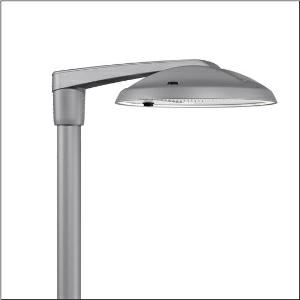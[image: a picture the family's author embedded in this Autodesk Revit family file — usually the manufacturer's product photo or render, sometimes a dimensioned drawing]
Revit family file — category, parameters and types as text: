
# Revit family: dl_r__50_iq_mini___st1_0a_5xa248d31y08ne_98a7
name_source: partatom
category: Lighting Fixtures
units: mm (PartAtom-declared; Revit-internal decimal feet)

## family parameters
Cut with Voids When Loaded = No
Host = Face
Light Source = No
Part Type = Normal
Room Calculation Point = No
Round Connector Dimension = Use Diameter
Shared = No

## types (1)
- --- (1 x LED, 17900 lm, 110.1 W, 3000K)
    Apparent Load = 110 VA
    CIE Flux Codes = 37 72 97 100 100
    Color Rendering = 70
    Color Temperature = 3000K
    Default Elevation = 1800 mm
    Description = DL® 50 iQ mini, mast luminaire, primary light control with lens, of PMMA, primary optical cover: cover, of toughened safety glass, transparent, light distribution: ST1.0a, light emission: direct distribution, primary light characteristic: asymmetric, installation type: post-top, side-entry, LED, High Power LED, rated luminous flux: 17.900lm, luminous efficacy: 163lm/W, light colour: 730, colour temperature: 3000K, control: optimised constant luminous flux control (CLO 2.0), Desk-Remote (wireless, voltage-free reading and setting of iQ features in the workshop via application-optimized NFC function/RFID function), Light-Fading, Smart-Wire, Night-Set, Lumen-Switch, Temp-Guard, Auto-Match, Street-Remote, presetting dimming logarithmic, mains connection: 230..240V, AC, 50/60Hz, connection cable pre-assembled, cable length: 10,5m, start of lifetime: 110W, end of service life: 116W, reduction: 50W, luminaire housing, of diecast aluminium, powder-coated, Siteco® metallic grey (DB 702S), inclination adjustable: 0°, 5°, 10° (post-top) | 0°, -5°, -10°, -15° (side-entry), please order mast post-top element or mast side-entry element separately, diameter: 500mm, height: 115mm, post-top: for spigot size d x l = 76 x 100mm; with reducer (optional accessory) 60 x 100mm | side-entry: for spigot size d x l = 60 x 100mm; with reducer (optional accessory) 42 x 100mm, Smart Interface below and above, protection rating (complete): IP66, insulation class (complete): insulation class II (safety insulation), certification: CE, ENEC, VDE, impact resistance: IK08, permissible operating ambient temperature for outdoor applications: -25..+40°C, standard-compliant lighting for roads and squares, packaging unit: 1 piece

Light Distribution: ST1.0a
    Height = 115 mm
    Lamp = 1 x LED
    Lamp Light Flux = 17900 lm
    Lamp Power = 110.1 W
    Lamp count = 1
    Length = 500 mm
    Luminous efficacy = 163 lm/W
    Manufacturer = Siteco
    ModVariant = No
    Model = 5XA248D31Y08NE
    Number of Poles = 1
    OnlyDefault = Yes
    Power Factor = 1
    Product Name = DL® 50 iQ mini | ST1.0a
    Product group = mast luminaire | pylon top
    ProductGroupID = 6100
    Protection Class = Protection class II
    Protection Degree = IP 66
    RLX_Detail_Level = 1
    RLX_Emergency_Light_Flux = 0 lm
    RLX_Emergency_Type = 0
    RLX_Emergency_Type_DB = No
    RlxData = <blob elided: 106601 chars, md5=6e95e681>
    Socket = socket
    Standby Power = 0 W
    System Light Flux = 17900 lm
    System Power = 110 W
    Type Comments = factory setting: luminous flux: 100 % | dim-lin: 254 | 601 mA
    Type Image = l_1251786.jpg
    URL = http://relux.com
    VarID = @adj_023841
    Voltage = 0 V
    Weight = 0.00 kg
    Width = 0 mm  [stored 0 ft]

note: [stored X ft] marks values corroborated as IEEE doubles in the binary element streams (Revit-internal decimal feet)

## geometry (parser evidence)
native form markers: Blend x4, Sweep x8
no freeform markers — native parametric forms only
